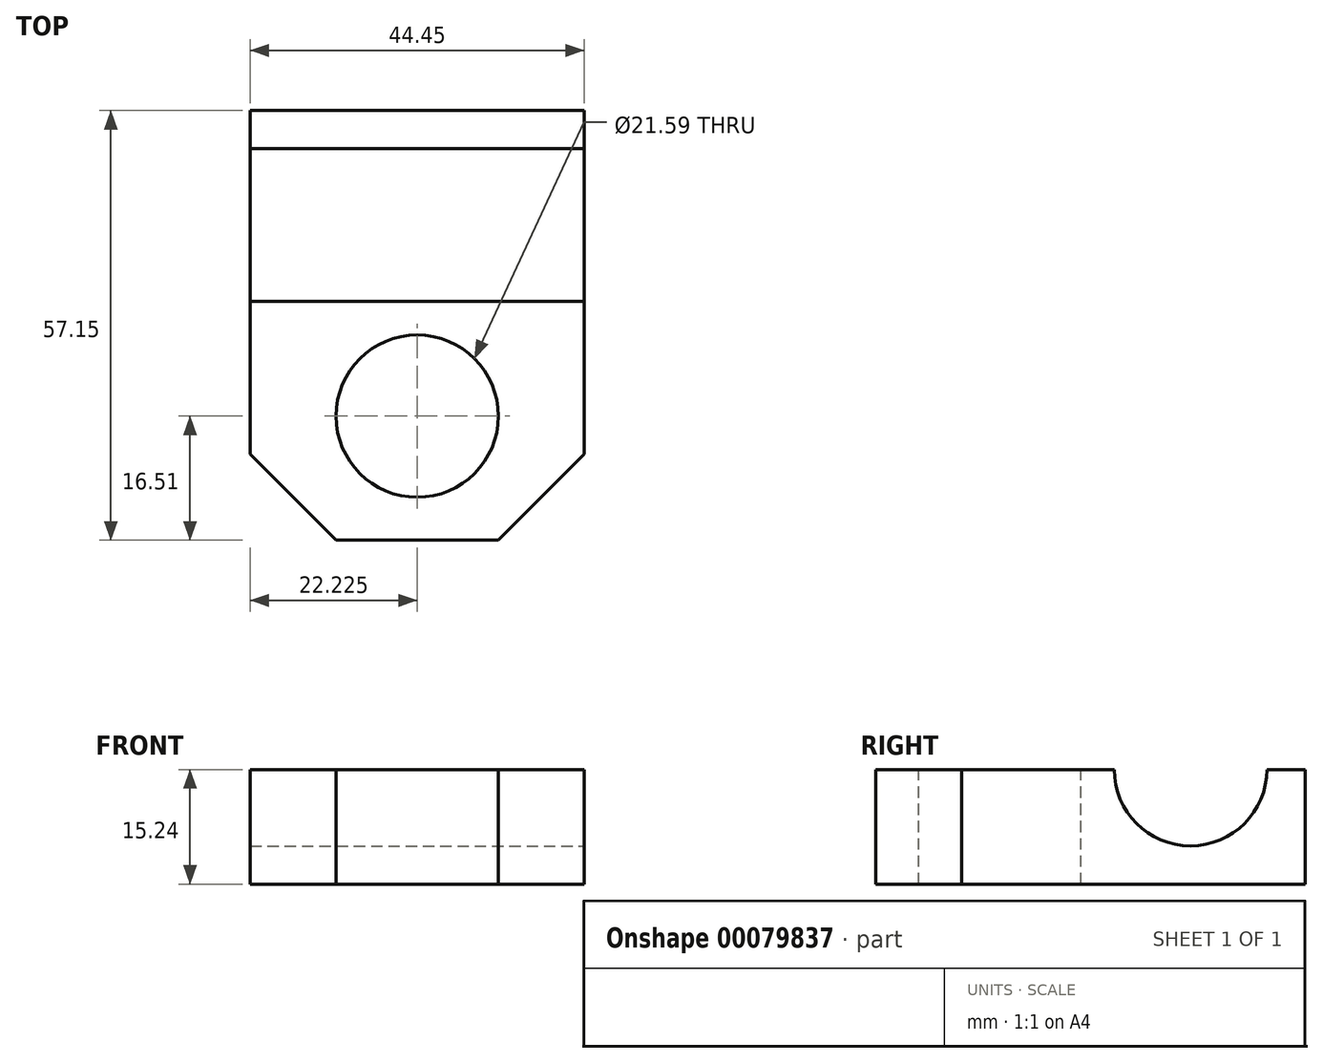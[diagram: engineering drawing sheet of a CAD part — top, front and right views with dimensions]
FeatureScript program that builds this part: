
annotation { "Feature Type Name" : "Feature", "Feature Type Description" : "" }
export const myFeature = defineFeature(function(context is Context, id is Id, definition is map)
    precondition{}
    {
        {
            var Q0;
            Q0=qCreatedBy(makeId("Top.planeOp"),FACE);
            var sketch = newSketch(context, id + "F0", { "sketchPlane" : qUnion([Q0])});
            skLineSegment(sketch, "E0", {"start": v(0, 0) * mm, "end": v(0, 57.15) * mm});
            skLineSegment(sketch, "E1", {"start": v(0, 57.15) * mm, "end": v(44.45, 57.15) * mm});
            skLineSegment(sketch, "E2", {"start": v(44.45, 57.15) * mm, "end": v(44.45, 0) * mm});
            skLineSegment(sketch, "E3", {"start": v(44.45, 0) * mm, "end": v(0, 0) * mm});
            skSolve(sketch);
        }
        {
            var Q0;
            Q0=makeQuery(id+"F0.imprint","IMPRINT",FACE,{"disambiguationData":[TD([[makeQuery(id+"F0.imprint","IMPRINT",EDGE,{"derivedFrom":sQuery(id+"F0.wireOp",EDGE,"E0")}),-1.0]])]});
            extrude(context, id + "F1", {"entities" : qUnion([Q0]), "depth" : 15.24 * mm});
        }
        {
            var Q0;
            Q0=makeQuery(id+"F1.opExtrude","SWEPT_EDGE",EDGE,{"disambiguationData":[OSD([sQuery(id+"F0.wireOp",EDGE,"E0"),sQuery(id+"F0.wireOp",EDGE,"E3")])]});
            var Q1;
            Q1=makeQuery(id+"F1.opExtrude","SWEPT_EDGE",EDGE,{"disambiguationData":[OSD([sQuery(id+"F0.wireOp",EDGE,"E2"),sQuery(id+"F0.wireOp",EDGE,"E3")])]});
            chamfer(context, id + "F2", {"entities" : qUnion([Q0, Q1]), "width" : 11.43 * mm, "tangentPropagation" : true});
        }
        {
            var Q0;
            Q0=makeQuery(id+"F1.opExtrude","CAP_FACE",FACE,{"disambiguationData":[OSD([sQuery(id+"F0.wireOp",EDGE,"E0"),sQuery(id+"F0.wireOp",EDGE,"E1"),sQuery(id+"F0.wireOp",EDGE,"E2"),sQuery(id+"F0.wireOp",EDGE,"E3")])],"isStart":false});
            var sketch = newSketch(context, id + "F3", { "sketchPlane" : qUnion([Q0])});
            skPoint(sketch, "E4", {"position": v(22.23, 16.51) * mm});
            skCircle(sketch, "E5", {"center": v(22.23, 16.51) * mm, "radius": 10.8 * mm});
            skSolve(sketch);
        }
        {
            var Q0;
            Q0=makeQuery(id+"F3.imprint","IMPRINT",FACE,{"disambiguationData":[TD([[makeQuery(id+"F3.imprint","IMPRINT",EDGE,{"derivedFrom":sQuery(id+"F3.wireOp",EDGE,"E5")}),1.0]])]});
            extrude(context, id + "F4", {"entities" : qUnion([Q0]), "operationType" : NewBodyOperationType.REMOVE, "oppositeDirection" : true, "depth" : 25.4 * mm});
        }
        {
            var Q0;
            Q0=makeQuery(id+"F1.opExtrude","SWEPT_FACE",FACE,{"disambiguationData":[OSD([sQuery(id+"F0.wireOp",EDGE,"E2")])]});
            var sketch = newSketch(context, id + "F5", { "sketchPlane" : qUnion([Q0])});
            skPoint(sketch, "E6", {"position": v(41.91, 15.24) * mm});
            skArc(sketch, "E7", {"start": v(31.75, 15.24) * mm, "mid": v(41.91, 5.08) * mm, "end": v(52.07, 15.24) * mm});
            skLineSegment(sketch, "E8", {"start": v(52.07, 15.24) * mm, "end": v(31.75, 15.24) * mm});
            skSolve(sketch);
        }
        {
            var Q0;
            {var subQ0=sQuery(id+"F5.wireOp",EDGE,"E7");var subQ1=makeQuery(id+"F1.opExtrude","CAP_EDGE",EDGE,{"disambiguationData":[OSD([sQuery(id+"F0.wireOp",EDGE,"E2")])],"isStart":false});var subQ2=makeQuery(id+"F5.imprint","INTERSECT",VERTEX,{"disambiguationData":[OD(0.0)],"derivedFrom":[subQ1,subQ0]});Q0=makeQuery(id+"F5.imprint","IMPRINT",FACE,{"disambiguationData":[TD([[makeQuery(id+"F5.imprint","IMPRINT",EDGE,{"disambiguationData":[TD([[subQ2,1.0]])],"derivedFrom":subQ0}),1.0]])]});}
            extrude(context, id + "F6", {"entities" : qUnion([Q0]), "operationType" : NewBodyOperationType.REMOVE, "oppositeDirection" : true, "depth" : 76.2 * mm});
        }
    });
